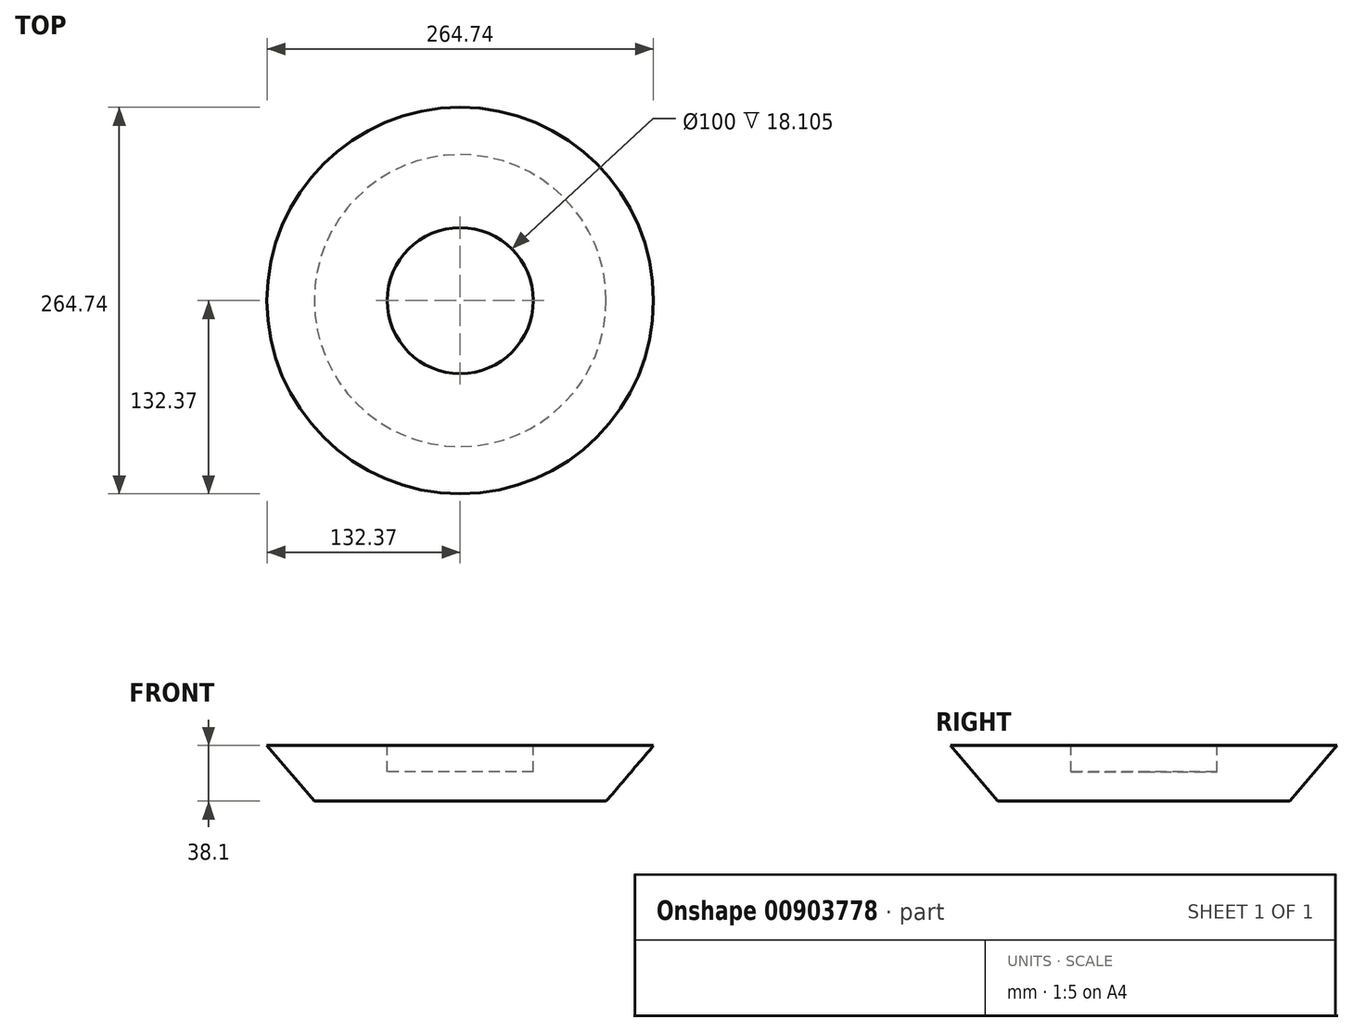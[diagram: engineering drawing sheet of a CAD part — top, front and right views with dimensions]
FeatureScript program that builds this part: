
annotation { "Feature Type Name" : "Feature", "Feature Type Description" : "" }
export const myFeature = defineFeature(function(context is Context, id is Id, definition is map)
    precondition{}
    {
        {
            var Q0;
            Q0=qCreatedBy(makeId("Right.planeOp"),FACE);
            var sketch = newSketch(context, id + "F0", { "sketchPlane" : qUnion([Q0])});
            skLineSegment(sketch, "E0", {"start": v(-132.37, 13.41) * mm, "end": v(-50, 13.41) * mm});
            skLineSegment(sketch, "E1", {"start": v(-50, 13.41) * mm, "end": v(-50, -4.7) * mm});
            skLineSegment(sketch, "E2", {"start": v(-50, -4.7) * mm, "end": v(0, -4.7) * mm});
            skLineSegment(sketch, "E3", {"start": v(0, -4.7) * mm, "end": v(0, -24.7) * mm});
            skLineSegment(sketch, "E4", {"start": v(0, -24.7) * mm, "end": v(-100, -24.7) * mm});
            skLineSegment(sketch, "E5", {"start": v(-100, -24.7) * mm, "end": v(-132.37, 13.41) * mm});
            skSolve(sketch);
        }
        {
            var Q0;
            Q0=makeQuery(id+"F0.imprint","IMPRINT",FACE,{"disambiguationData":[TD([[makeQuery(id+"F0.imprint","IMPRINT",EDGE,{"derivedFrom":sQuery(id+"F0.wireOp",EDGE,"E0")}),-1.0]])]});
            var Q1;
            Q1=sQuery(id+"F0.wireOp",EDGE,"E3");
            revolve(context, id + "F1", {"surfaceOperationType" : NewSurfaceOperationType.NEW, "entities" : qUnion([Q0]), "axis" : qUnion([Q1]), "revolveType" : RevolveType.FULL});
        }
    });
